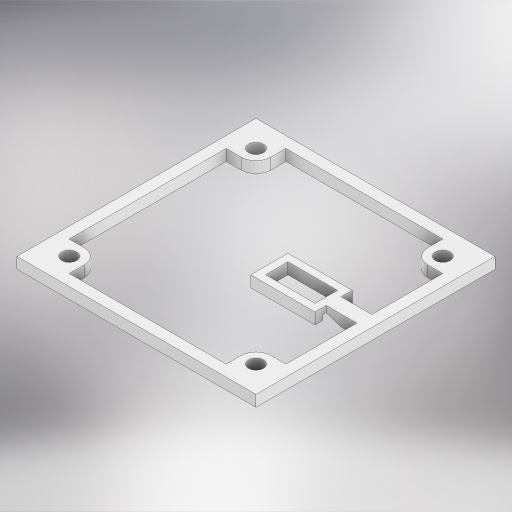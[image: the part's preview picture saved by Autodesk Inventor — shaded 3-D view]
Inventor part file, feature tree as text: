
AUTODESK INVENTOR PART (.ipt)
format: ipt  version: 2024 (Build 280153000, 153)  size: 402,432 bytes
history: native  units: in
note: dims shown in document units (in); Inventor stores cm internally (conversion verified against a paired STEP export)
features: extrude x3, sketch x3, plane x2, pattern_circular x1, chamfer x1, other x1
ambient origin geometry x8: Origin, YZ Plane, XZ Plane, XY Plane, X Axis, Y Axis, Z Axis, Center Point
bodies: Body1 (feature_tree)
feature tree (11):
  extrude  "Extrusion3"  Depth=4.0in
  extrude  "Extrusion4"  Depth=0.1875in TaperAngle=0.0deg
  pattern_circular  "Circular Pattern1"  [2 undecoded]
  extrude  "Extrusion5"  Depth=0.1875in
  chamfer  "Chamfer1"  Distance=0.25in
  other  "Work Axis1"
  sketch  "Sketch3"  dims[d17=4.0in d18=4.0in]
  sketch  "Sketch4"  dims[d19=0.1875in d20=0.1875in d21=0.0in]
  sketch  "Sketch5"  dims[d22=4.0in d23=4.0in d24=0.1875in d25=0.25in d26=0.125in d27=0.1875in d28=0.0in d30=1.5748in d31=360.0deg d33=0.1378in d34=0.7874in d35=3.625in d36=0.1875in d37=0.0in d38=0.0197in d39=0.125in d69=0.375in d70=0.125in d71=45.0deg d72=1.0in d73=0.1555in d74=0.3346in d75=0.25in d16=0.0312in]
  plane  "Work Plane2"
  plane  "Work Plane3"
note: 2 required parameter values undecoded (feature->parameter linkage not recoverable at this tier; creation-order binding heuristic only, values carry confidence <= 0.55)
